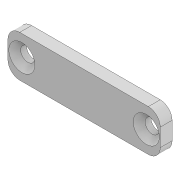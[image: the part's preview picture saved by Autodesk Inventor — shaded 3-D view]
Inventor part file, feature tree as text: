
AUTODESK INVENTOR PART (.ipt)
format: ipt  version: 2021 (Build 250183000, 183)  size: 99,840 bytes
history: native  units: mm
features: other x6, reference x3, sketch x2, extrude x1, hole x1
ambient origin geometry x8: Origin, YZ Plane, XZ Plane, XY Plane, X Axis, Y Axis, Z Axis, Center Point
bodies: Body1 (feature_tree)
feature tree (13):
  other  "Твердое тело1"
  other  "РабПлоскость1"
  extrude  "Выдавливание1"  Depth=2.0mm TaperAngle=0.0deg
  hole  "Отверстие1"  [1 undecoded]
  sketch  "Эскиз1"
  reference  "Ссылка1"
  sketch  "Эскиз2"
  reference  "Ссылка2"
  reference  "Ссылка3"
  other  "<userpath>\Desktop\теплица\датчики почва воздух\Компоновка.iam"
  other  "Компоновка.iam"
  other  "Кронштейн МК:1"
  other  "Capacative Soil Moisture Sensor:1"
note: 1 required parameter value undecoded (feature->parameter linkage not recoverable at this tier; creation-order binding heuristic only, values carry confidence <= 0.55)
